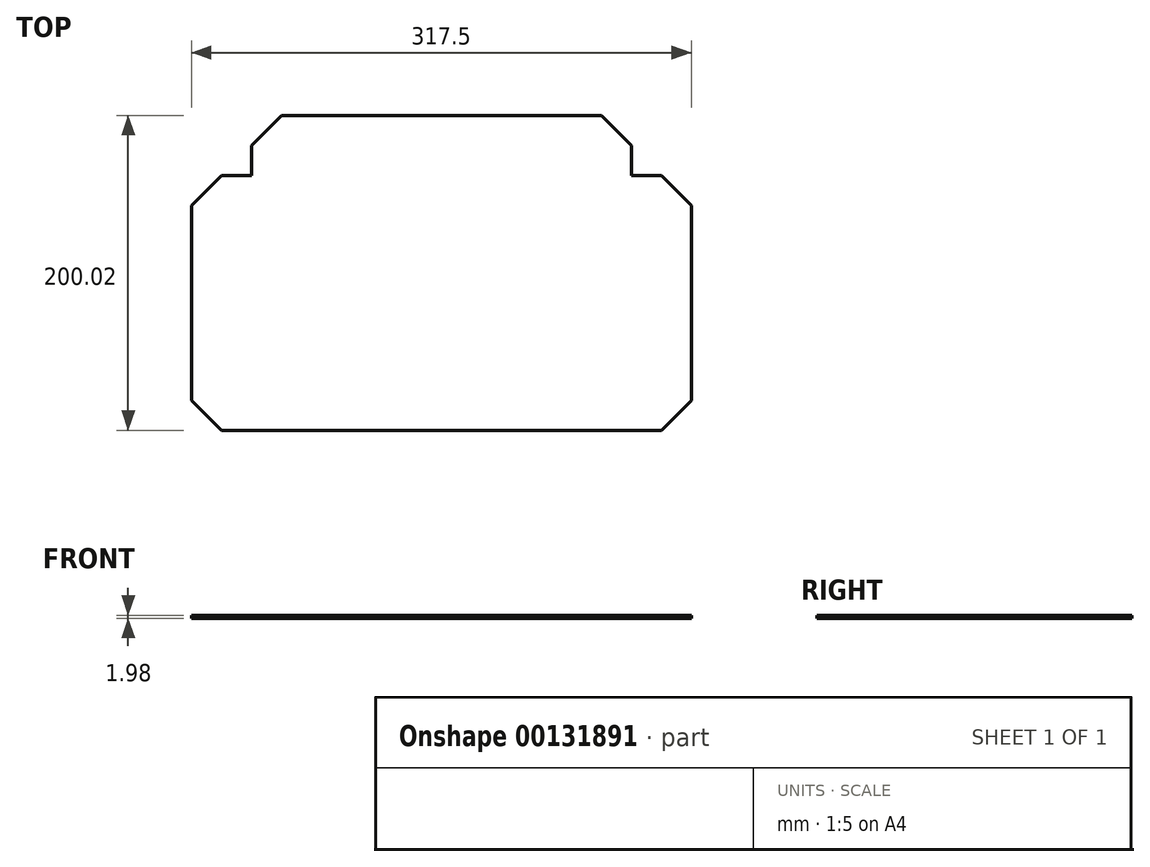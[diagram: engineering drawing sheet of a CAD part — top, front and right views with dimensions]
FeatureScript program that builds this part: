
annotation { "Feature Type Name" : "Feature", "Feature Type Description" : "" }
export const myFeature = defineFeature(function(context is Context, id is Id, definition is map)
    precondition{}
    {
        {
            var Q0;
            Q0=qCreatedBy(makeId("Top.planeOp"),FACE);
            var sketch = newSketch(context, id + "F0", { "sketchPlane" : qUnion([Q0])});
            skLineSegment(sketch, "E0.bottom", {"start": v(120.65, -80.96) * mm, "end": v(-120.65, -80.96) * mm});
            skLineSegment(sketch, "E0.top", {"start": v(120.65, 80.96) * mm, "end": v(-120.65, 80.96) * mm});
            skLineSegment(sketch, "E0.left", {"start": v(120.65, -80.96) * mm, "end": v(120.65, 80.96) * mm});
            skLineSegment(sketch, "E0.right", {"start": v(-120.65, -80.96) * mm, "end": v(-120.65, 80.96) * mm});
            skPoint(sketch, "E0.middle", {"position": v(0, 0) * mm});
            skLineSegment(sketch, "E1", {"start": v(120.65, -80.96) * mm, "end": v(139.7, -80.96) * mm});
            skLineSegment(sketch, "E2", {"start": v(139.7, -80.96) * mm, "end": v(139.7, 80.96) * mm});
            skLineSegment(sketch, "E3", {"start": v(139.7, 80.96) * mm, "end": v(120.65, 80.96) * mm});
            skLineSegment(sketch, "E4", {"start": v(120.65, 80.96) * mm, "end": v(120.65, 100.01) * mm});
            skLineSegment(sketch, "E5", {"start": v(120.65, 100.01) * mm, "end": v(-120.65, 100.01) * mm});
            skLineSegment(sketch, "E6", {"start": v(-120.65, 100.01) * mm, "end": v(-120.65, 80.96) * mm});
            skLineSegment(sketch, "E7", {"start": v(101.6, 119.06) * mm, "end": v(-101.6, 119.06) * mm});
            skLineSegment(sketch, "E8", {"start": v(-120.65, 100.01) * mm, "end": v(-101.6, 119.06) * mm});
            skPoint(sketch, "E9.orphan", {"position": v(-120.65, 119.06) * mm});
            skLineSegment(sketch, "E10", {"start": v(120.65, 100.01) * mm, "end": v(101.6, 119.06) * mm});
            skLineSegment(sketch, "E11", {"start": v(139.7, -80.96) * mm, "end": v(158.75, -61.91) * mm});
            skLineSegment(sketch, "E12", {"start": v(139.7, 80.96) * mm, "end": v(158.75, 61.91) * mm});
            skPoint(sketch, "E13.orphan", {"position": v(159.87, -80.96) * mm});
            skLineSegment(sketch, "E14", {"start": v(158.75, 61.91) * mm, "end": v(158.75, -61.91) * mm});
            skLineSegment(sketch, "E15.MirrorCS", {"start": v(-120.65, -80.96) * mm, "end": v(-139.7, -80.96) * mm});
            skLineSegment(sketch, "E16.MirrorCS", {"start": v(-139.7, 80.96) * mm, "end": v(-120.65, 80.96) * mm});
            skLineSegment(sketch, "E17.MirrorCS", {"start": v(-139.7, -80.96) * mm, "end": v(-158.75, -61.91) * mm});
            skLineSegment(sketch, "E18.MirrorCS", {"start": v(-139.7, 80.96) * mm, "end": v(-158.75, 61.91) * mm});
            skPoint(sketch, "E19.MirrorP", {"position": v(-159.87, -80.96) * mm});
            skLineSegment(sketch, "E20.MirrorCS", {"start": v(-139.7, -80.96) * mm, "end": v(-139.7, 80.96) * mm});
            skLineSegment(sketch, "E21.MirrorCS", {"start": v(-158.75, 61.91) * mm, "end": v(-158.75, -61.91) * mm});
            skSolve(sketch);
        }
        {
            var Q0;
            Q0 = qSketchRegion(id + "F0", true);
            extrude(context, id + "F1", {"entities" : qUnion([Q0]), "depth" : 1.98 * mm});
        }
    });
